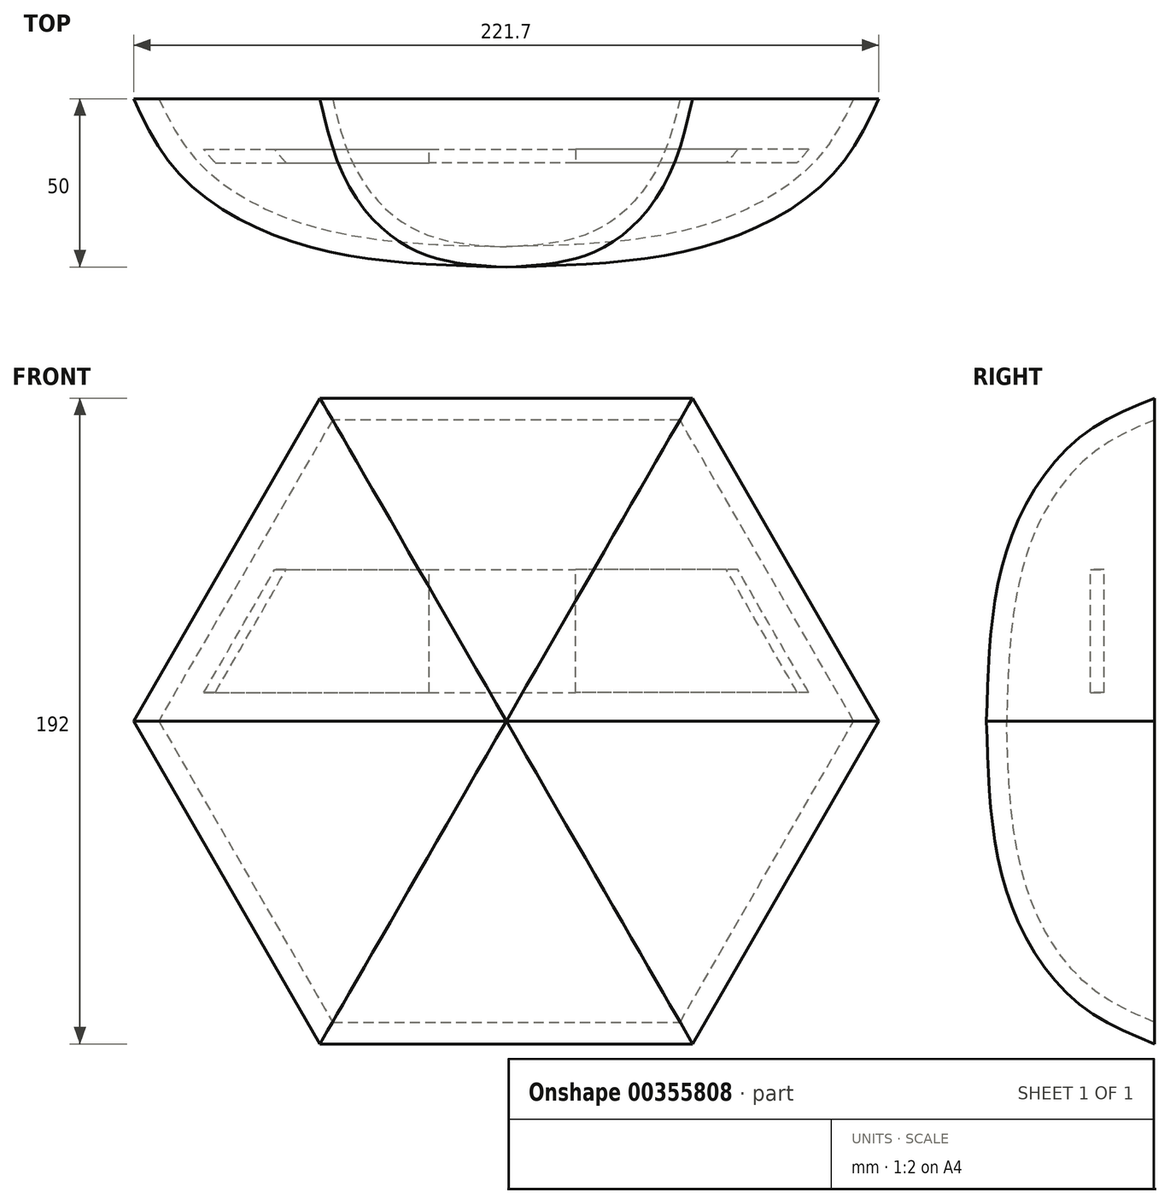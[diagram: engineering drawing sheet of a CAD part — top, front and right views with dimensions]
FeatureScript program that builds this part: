
annotation { "Feature Type Name" : "Feature", "Feature Type Description" : "" }
export const myFeature = defineFeature(function(context is Context, id is Id, definition is map)
    precondition{}
    {
        {
            var Q0;
            Q0=qCreatedBy(makeId("Front.planeOp"),FACE);
            var sketch = newSketch(context, id + "F0", { "sketchPlane" : qUnion([Q0])});
            skCircle(sketch, "E0.cCircle", {"center": v(0, 0) * mm, "radius": 96 * mm, "construction": true});
            skLineSegment(sketch, "E0.0", {"start": v(-55.43, 96) * mm, "end": v(55.43, 96) * mm});
            skLineSegment(sketch, "E0.1", {"start": v(55.43, 96) * mm, "end": v(110.85, 0) * mm});
            skLineSegment(sketch, "E0.2", {"start": v(110.85, 0) * mm, "end": v(55.43, -96) * mm});
            skLineSegment(sketch, "E0.3", {"start": v(55.43, -96) * mm, "end": v(-55.43, -96) * mm});
            skLineSegment(sketch, "E0.4", {"start": v(-55.43, -96) * mm, "end": v(-110.85, 0) * mm});
            skLineSegment(sketch, "E0.5", {"start": v(-110.85, 0) * mm, "end": v(-55.43, 96) * mm});
            skPoint(sketch, "E0.0.midPoint", {"position": v(0, 96) * mm});
            skSolve(sketch);
        }
        {
            var Q0;
            Q0=qCreatedBy(makeId("Front.planeOp"),FACE);
            cPlane(context, id + "F1", {"entities" : qUnion([Q0]), "cplaneType" : CPlaneType.OFFSET, "offset" : 20 * mm, "width" : 150 * mm, "height" : 150 * mm});
        }
        {
            var Q0;
            Q0=qCreatedBy(id+"F1.planeOp",FACE);
            var sketch = newSketch(context, id + "F2", { "sketchPlane" : qUnion([Q0])});
            skCircle(sketch, "E1.cCircle", {"center": v(0, 0) * mm, "radius": 86 * mm, "construction": true});
            skLineSegment(sketch, "E1.0", {"start": v(-49.65, 86) * mm, "end": v(49.65, 86) * mm});
            skLineSegment(sketch, "E1.1", {"start": v(49.65, 86) * mm, "end": v(99.3, 0) * mm});
            skLineSegment(sketch, "E1.2", {"start": v(99.3, 0) * mm, "end": v(49.65, -86) * mm});
            skLineSegment(sketch, "E1.3", {"start": v(49.65, -86) * mm, "end": v(-49.65, -86) * mm});
            skLineSegment(sketch, "E1.4", {"start": v(-49.65, -86) * mm, "end": v(-99.3, 0) * mm});
            skLineSegment(sketch, "E1.5", {"start": v(-99.3, 0) * mm, "end": v(-49.65, 86) * mm});
            skPoint(sketch, "E1.0.midPoint", {"position": v(0, 86) * mm});
            skSolve(sketch);
        }
        {
            var Q0;
            Q0=qCreatedBy(id+"F1.planeOp",FACE);
            cPlane(context, id + "F3", {"entities" : qUnion([Q0]), "cplaneType" : CPlaneType.OFFSET, "offset" : 20 * mm, "width" : 150 * mm, "height" : 150 * mm});
        }
        {
            var Q0;
            Q0=qCreatedBy(id+"F3.planeOp",FACE);
            var sketch = newSketch(context, id + "F4", { "sketchPlane" : qUnion([Q0])});
            skCircle(sketch, "E2.cCircle", {"center": v(0, 0) * mm, "radius": 61 * mm, "construction": true});
            skLineSegment(sketch, "E2.0", {"start": v(-35.22, 61) * mm, "end": v(35.22, 61) * mm});
            skLineSegment(sketch, "E2.1", {"start": v(35.22, 61) * mm, "end": v(70.44, 0) * mm});
            skLineSegment(sketch, "E2.2", {"start": v(70.44, 0) * mm, "end": v(35.22, -61) * mm});
            skLineSegment(sketch, "E2.3", {"start": v(35.22, -61) * mm, "end": v(-35.22, -61) * mm});
            skLineSegment(sketch, "E2.4", {"start": v(-35.22, -61) * mm, "end": v(-70.44, 0) * mm});
            skLineSegment(sketch, "E2.5", {"start": v(-70.44, 0) * mm, "end": v(-35.22, 61) * mm});
            skPoint(sketch, "E2.0.midPoint", {"position": v(0, 61) * mm});
            skSolve(sketch);
        }
        {
            var Q0;
            Q0=qCreatedBy(id+"F3.planeOp",FACE);
            cPlane(context, id + "F5", {"entities" : qUnion([Q0]), "cplaneType" : CPlaneType.OFFSET, "offset" : 10 * mm, "width" : 150 * mm, "height" : 150 * mm});
        }
        {
            var Q0;
            Q0=qCreatedBy(id+"F5.planeOp",FACE);
            var sketch = newSketch(context, id + "F6", { "sketchPlane" : qUnion([Q0])});
            skPoint(sketch, "E3", {"position": v(0, 0) * mm});
            skSolve(sketch);
        }
        {
            var Q0;
            Q0=makeQuery(id+"F0.imprint","IMPRINT",FACE,{"disambiguationData":[TD([[makeQuery(id+"F0.imprint","IMPRINT",EDGE,{"derivedFrom":sQuery(id+"F0.wireOp",EDGE,"E0.0")}),-1.0]])]});
            var Q1;
            Q1=makeQuery(id+"F2.imprint","IMPRINT",FACE,{"disambiguationData":[TD([[makeQuery(id+"F2.imprint","IMPRINT",EDGE,{"derivedFrom":sQuery(id+"F2.wireOp",EDGE,"E1.0")}),-1.0]])]});
            var Q2;
            Q2=makeQuery(id+"F4.imprint","IMPRINT",FACE,{"disambiguationData":[TD([[makeQuery(id+"F4.imprint","IMPRINT",EDGE,{"derivedFrom":sQuery(id+"F4.wireOp",EDGE,"E2.0")}),-1.0]])]});
            var Q3;
            Q3=sQuery(id+"F6.wireOp",VERTEX,"E3");
            loft(context, id + "F7", {"sheetProfilesArray" : [{ "sheetProfileEntities" : qUnion([Q0]) }, { "sheetProfileEntities" : qUnion([Q1]) }, { "sheetProfileEntities" : qUnion([Q2]) }, { "sheetProfileEntities" : qUnion([Q3]) }]});
        }
        {
            var Q0;
            Q0=makeQuery(id+"F7.opLoft","CAP_FACE",FACE,{"disambiguationData":[OSD([makeQuery(id+"F0.imprint","IMPRINT",FACE,{"disambiguationData":[TD([[makeQuery(id+"F0.imprint","IMPRINT",EDGE,{"derivedFrom":sQuery(id+"F0.wireOp",EDGE,"E0.0")}),-1.0]])]})])],"isStart":true});
            shell(context, id + "F8", {"entities" : qUnion([Q0]), "thickness" : 6 * mm});
        }
        {
            var Q0;
            Q0=qCreatedBy(makeId("Top.planeOp"),FACE);
            cPlane(context, id + "F9", {"entities" : qUnion([Q0]), "cplaneType" : CPlaneType.OFFSET, "offset" : 45 * mm, "width" : 150 * mm, "height" : 150 * mm});
        }
        {
            var Q0;
            Q0=qCreatedBy(id+"F9.planeOp",FACE);
            var sketch = newSketch(context, id + "F10", { "sketchPlane" : qUnion([Q0])});
            skLineSegment(sketch, "E4", {"start": v(-22.97, -15) * mm, "end": v(20.65, -15) * mm});
            skLineSegment(sketch, "E5", {"start": v(20.65, -15) * mm, "end": v(20.65, -19) * mm});
            skLineSegment(sketch, "E6", {"start": v(20.65, -19) * mm, "end": v(-22.97, -19) * mm});
            skLineSegment(sketch, "E7", {"start": v(-22.97, -19) * mm, "end": v(-22.97, -15) * mm});
            skSolve(sketch);
        }
        {
            var Q0;
            Q0=qSketchRegion(id+"F10",true);
            extrude(context, id + "F11", {"entities" : qUnion([Q0]), "oppositeDirection" : true, "depth" : 36.5 * mm});
        }
        {
            var Q0;
            Q0=makeQuery(id+"F11.opExtrude","SWEPT_FACE",FACE,{"disambiguationData":[OSD([sQuery(id+"F10.wireOp",EDGE,"E5")])]});
            extrude(context, id + "F12", {"entities" : qUnion([Q0]), "endBound" : BoundingType.UP_TO_NEXT, "depth" : 25 * mm});
        }
        {
            var Q0;
            Q0=makeQuery(id+"F11.opExtrude","SWEPT_FACE",FACE,{"disambiguationData":[OSD([sQuery(id+"F10.wireOp",EDGE,"E7")])]});
            extrude(context, id + "F13", {"entities" : qUnion([Q0]), "endBound" : BoundingType.UP_TO_NEXT, "depth" : 25 * mm});
        }
    });
